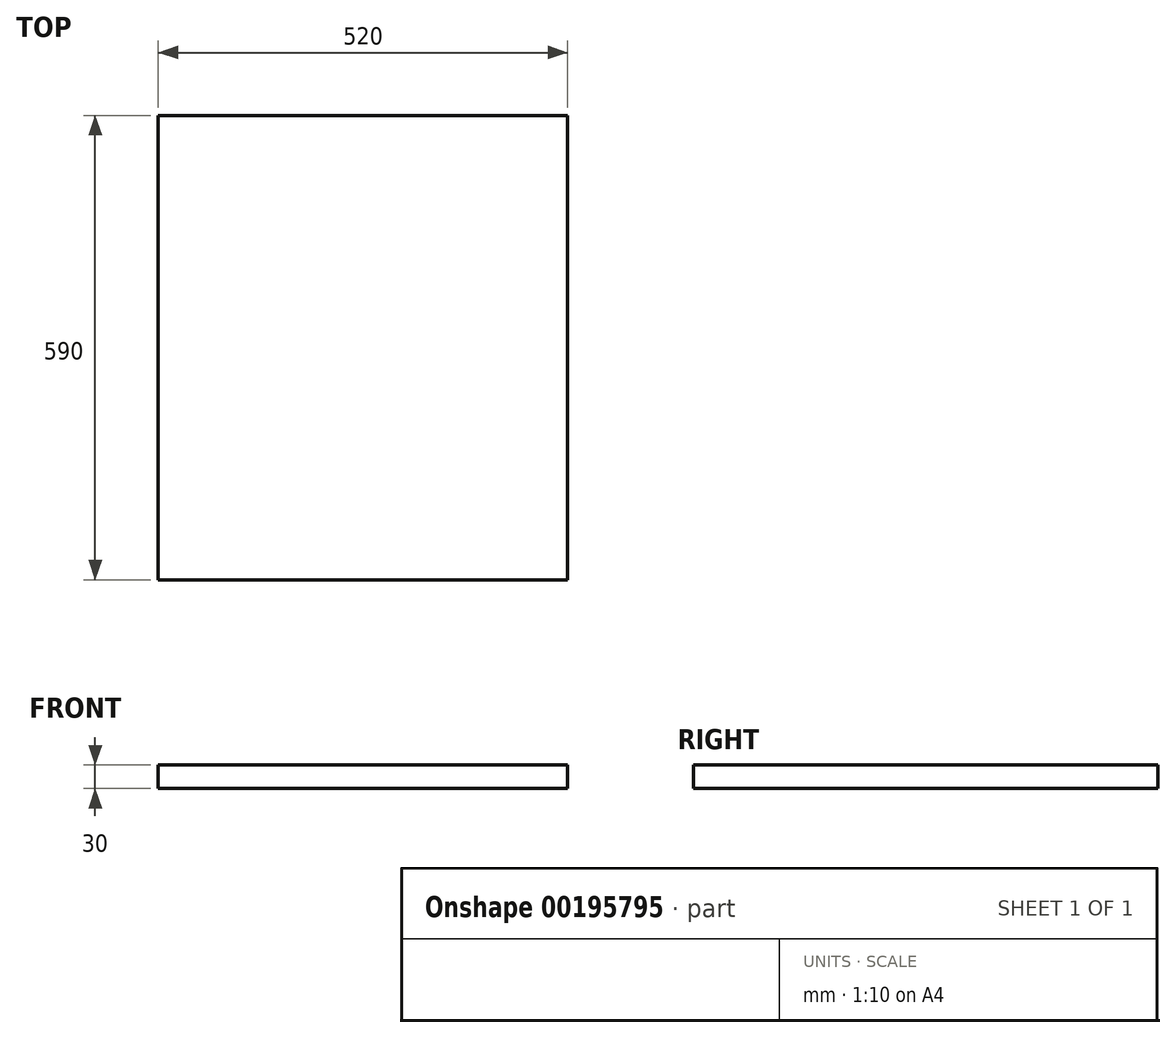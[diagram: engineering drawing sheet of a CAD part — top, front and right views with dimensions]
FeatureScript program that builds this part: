
annotation { "Feature Type Name" : "Feature", "Feature Type Description" : "" }
export const myFeature = defineFeature(function(context is Context, id is Id, definition is map)
    precondition{}
    {
        {
            var Q0;
            Q0=qCreatedBy(makeId("Top.planeOp"),FACE);
            var sketch = newSketch(context, id + "F0", { "sketchPlane" : qUnion([Q0])});
            skLineSegment(sketch, "E0.bottom", {"start": v(-332.65, -196.68) * mm, "end": v(187.35, -196.68) * mm});
            skLineSegment(sketch, "E0.top", {"start": v(-332.65, 393.32) * mm, "end": v(187.35, 393.32) * mm});
            skLineSegment(sketch, "E0.left", {"start": v(-332.65, -196.68) * mm, "end": v(-332.65, 393.32) * mm});
            skLineSegment(sketch, "E0.right", {"start": v(187.35, -196.68) * mm, "end": v(187.35, 393.32) * mm});
            skSolve(sketch);
        }
        {
            var Q0;
            Q0=makeQuery(id+"F0.imprint","IMPRINT",FACE,{"disambiguationData":[TD([[makeQuery(id+"F0.imprint","IMPRINT",EDGE,{"derivedFrom":sQuery(id+"F0.wireOp",EDGE,"E0.bottom")}),1.0]])]});
            extrude(context, id + "F1", {"entities" : qUnion([Q0]), "depth" : 30 * mm});
        }
    });
